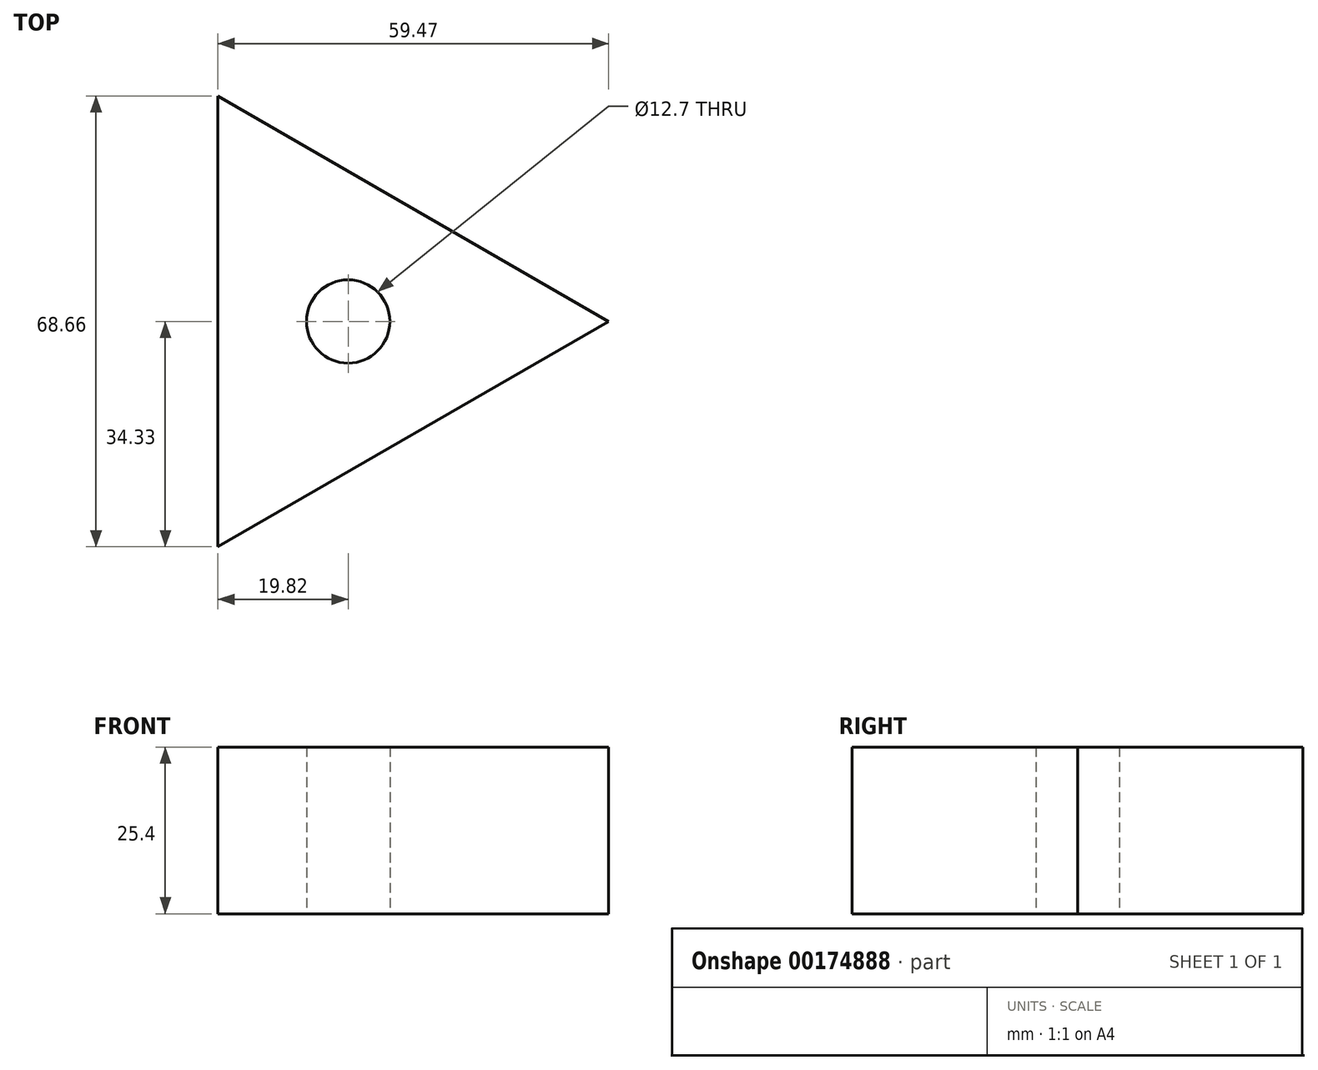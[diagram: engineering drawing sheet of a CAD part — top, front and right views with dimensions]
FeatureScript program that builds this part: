
annotation { "Feature Type Name" : "Feature", "Feature Type Description" : "" }
export const myFeature = defineFeature(function(context is Context, id is Id, definition is map)
    precondition{}
    {
        {
            var Q0;
            Q0=qCreatedBy(makeId("Top.planeOp"),FACE);
            var sketch = newSketch(context, id + "F0", { "sketchPlane" : qUnion([Q0])});
            skCircle(sketch, "E0.cCircle", {"center": v(0, 0) * mm, "radius": 48.01 * mm, "construction": true});
            skLineSegment(sketch, "E0.0", {"start": v(48.01, 83.16) * mm, "end": v(48.01, -83.16) * mm});
            skLineSegment(sketch, "E0.1", {"start": v(48.01, -83.16) * mm, "end": v(-96.02, 0) * mm});
            skLineSegment(sketch, "E0.2", {"start": v(-96.02, 0) * mm, "end": v(48.01, 83.16) * mm});
            skPoint(sketch, "E0.0.midPoint", {"position": v(48.01, 0) * mm});
            skSolve(sketch);
        }
        {
            var Q0;
            Q0=makeQuery(id+"F0.imprint","IMPRINT",FACE,{"disambiguationData":[TD([[makeQuery(id+"F0.imprint","IMPRINT",EDGE,{"derivedFrom":sQuery(id+"F0.wireOp",EDGE,"E0.0")}),-1.0]])]});
            extrude(context, id + "F1", {"entities" : qUnion([Q0]), "depth" : 25.4 * mm});
        }
        {
            var Q0;
            Q0=sQuery(id+"F0.wireOp",VERTEX,"E0.cCircle.center");
            var Q1;
            Q1=makeQuery(id+"F1.opExtrude","SWEPT_BODY",BODY,{"disambiguationData":[OSD([sQuery(id+"F0.wireOp",EDGE,"E0.0"),sQuery(id+"F0.wireOp",EDGE,"E0.1"),sQuery(id+"F0.wireOp",EDGE,"E0.2")])]});
            hole(context, id + "F2", {"style" : HoleStyle.SIMPLE, "endStyle" : HoleEndStyle.THROUGH, "oppositeDirection" : true, "holeDiameter" : 12.7 * mm, "locations" : qUnion([Q0]), "scope" : qUnion([Q1]), "isTappedThrough" : true});
        }
        {
            var Q0;
            Q0=makeQuery(id+"F1.opExtrude","SWEPT_EDGE",EDGE,{"disambiguationData":[OSD([sQuery(id+"F0.wireOp",EDGE,"E0.0"),sQuery(id+"F0.wireOp",EDGE,"E0.1")])]});
            var Q1;
            Q1=makeQuery(id+"F1.opExtrude","SWEPT_EDGE",EDGE,{"disambiguationData":[OSD([sQuery(id+"F0.wireOp",EDGE,"E0.0"),sQuery(id+"F0.wireOp",EDGE,"E0.2")])]});
            var Q2;
            Q2=makeQuery(id+"F1.opExtrude","SWEPT_EDGE",EDGE,{"disambiguationData":[OSD([sQuery(id+"F0.wireOp",EDGE,"E0.1"),sQuery(id+"F0.wireOp",EDGE,"E0.2")])]});
            chamfer(context, id + "F3", {"entities" : qUnion([Q0, Q1, Q2]), "width" : 50.8 * mm, "tangentPropagation" : true});
        }
    });
